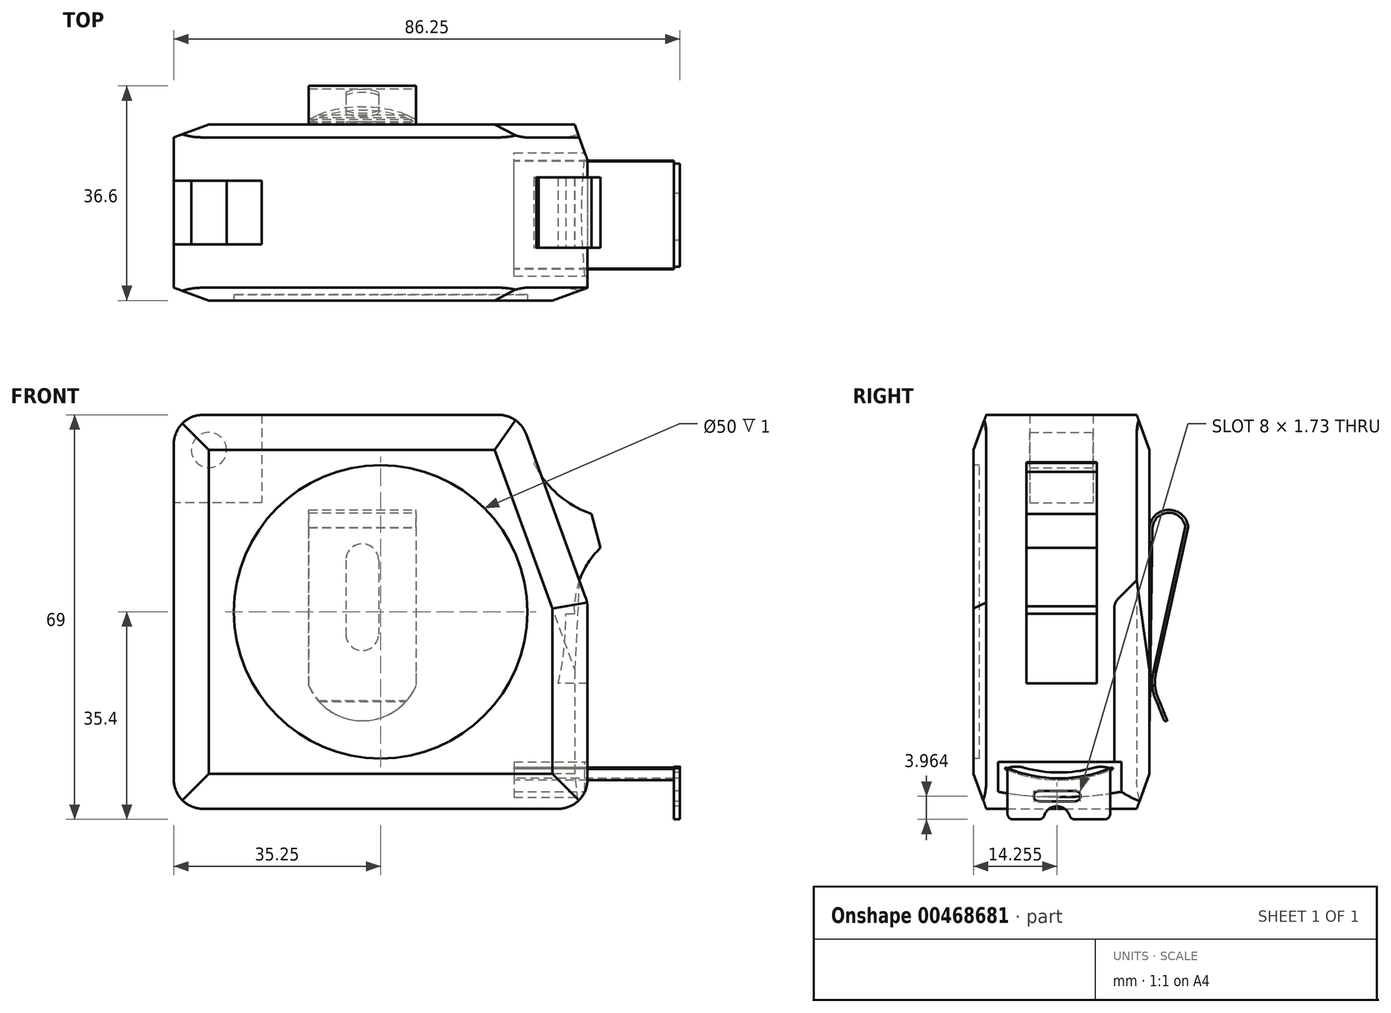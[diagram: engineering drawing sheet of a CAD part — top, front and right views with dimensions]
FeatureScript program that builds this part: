
annotation { "Feature Type Name" : "Feature", "Feature Type Description" : "" }
export const myFeature = defineFeature(function(context is Context, id is Id, definition is map)
    precondition{}
    {
        {
            var Q0;
            Q0=qCreatedBy(makeId("Front.planeOp"),FACE);
            var sketch = newSketch(context, id + "F0", { "sketchPlane" : qUnion([Q0])});
            skLineSegment(sketch, "E0.bottom", {"start": v(35.25, -33.6) * mm, "end": v(-35.25, -33.6) * mm});
            skLineSegment(sketch, "E0.top", {"start": v(35.25, 33.6) * mm, "end": v(-35.25, 33.6) * mm});
            skLineSegment(sketch, "E0.left", {"start": v(35.25, -33.6) * mm, "end": v(35.25, 33.6) * mm});
            skLineSegment(sketch, "E0.right", {"start": v(-35.25, -33.6) * mm, "end": v(-35.25, 33.6) * mm});
            skPoint(sketch, "E0.middle", {"position": v(0, 0) * mm});
            skSolve(sketch);
        }
        {
            var Q0;
            Q0 = qSketchRegion(id + "F0", true);
            extrude(context, id + "F1", {"entities" : qUnion([Q0]), "endBound" : BoundingType.SYMMETRIC, "depth" : 30 * mm});
        }
        {
            var Q0;
            Q0=makeQuery(id+"F1.opExtrude","SWEPT_EDGE",EDGE,{"disambiguationData":[OSD([sQuery(id+"F0.wireOp",EDGE,"E0.top"),sQuery(id+"F0.wireOp",EDGE,"E0.left")])]});
            chamfer(context, id + "F2", {"entities" : qUnion([Q0]), "chamferType" : ChamferType.OFFSET_ANGLE, "width" : 32 * mm, "oppositeDirection" : true, "angle" : 20 * degree, "tangentPropagation" : true});
        }
        {
            var Q0;
            Q0=makeQuery(id+"F1.opExtrude","CAP_FACE",FACE,{"disambiguationData":[OSD([sQuery(id+"F0.wireOp",EDGE,"E0.bottom"),sQuery(id+"F0.wireOp",EDGE,"E0.top"),sQuery(id+"F0.wireOp",EDGE,"E0.left"),sQuery(id+"F0.wireOp",EDGE,"E0.right")])],"isStart":false});
            var sketch = newSketch(context, id + "F3", { "sketchPlane" : qUnion([Q0])});
            skCircle(sketch, "E1", {"center": v(0, 0) * mm, "radius": 25 * mm});
            skSolve(sketch);
        }
        {
            var Q0;
            Q0 = qSketchRegion(id + "F3", true);
            extrude(context, id + "F4", {"entities" : qUnion([Q0]), "operationType" : NewBodyOperationType.REMOVE, "oppositeDirection" : true, "depth" : 1 * mm});
        }
        {
            var Q0;
            Q0=makeQuery(id+"F1.opExtrude","CAP_FACE",FACE,{"disambiguationData":[OSD([sQuery(id+"F0.wireOp",EDGE,"E0.bottom"),sQuery(id+"F0.wireOp",EDGE,"E0.top"),sQuery(id+"F0.wireOp",EDGE,"E0.left"),sQuery(id+"F0.wireOp",EDGE,"E0.right")])],"isStart":true});
            var sketch = newSketch(context, id + "F5", { "sketchPlane" : qUnion([Q0])});
            skLineSegment(sketch, "E2.bottom", {"start": v(-6.05, 17.4) * mm, "end": v(12.25, 17.4) * mm});
            skLineSegment(sketch, "E2.left", {"start": v(-6.05, 17.4) * mm, "end": v(-6.05, -12.6) * mm});
            skLineSegment(sketch, "E2.right", {"start": v(12.25, 17.4) * mm, "end": v(12.25, -12.6) * mm});
            skArc(sketch, "E3", {"start": v(-6.05, -12.6) * mm, "mid": v(3.1, -18.6) * mm, "end": v(12.25, -12.6) * mm});
            skLineSegment(sketch, "E4.left", {"start": v(5.93, -3.8) * mm, "end": v(5.93, 8.8) * mm});
            skLineSegment(sketch, "E4.right", {"start": v(0.35, -3.8) * mm, "end": v(0.35, 8.8) * mm});
            skPoint(sketch, "E4.middle", {"position": v(3.14, 2.5) * mm});
            skArc(sketch, "E5", {"start": v(0.35, -3.8) * mm, "mid": v(3.14, -6.6) * mm, "end": v(5.93, -3.8) * mm});
            skArc(sketch, "E6", {"start": v(0.35, 8.8) * mm, "mid": v(3.14, 11.6) * mm, "end": v(5.93, 8.8) * mm});
            skSolve(sketch);
        }
        {
            var Q0;
            Q0 = qSketchRegion(id + "F5", true);
            extrude(context, id + "F6", {"entities" : qUnion([Q0]), "operationType" : NewBodyOperationType.ADD, "depth" : 6.6 * mm});
        }
        {
            var Q0;
            Q0=makeQuery(id+"F6.opExtrude","SWEPT_FACE",FACE,{"disambiguationData":[OSD([sQuery(id+"F5.wireOp",EDGE,"E2.left")])]});
            var sketch = newSketch(context, id + "F7", { "sketchPlane" : qUnion([Q0])});
            skSolve(sketch);
        }
        {
            var Q0;
            {var subQ0=sQuery(id+"F5.wireOp",EDGE,"E2.left");Q0=makeQuery(id+"F7.imprint","IMPRINT",FACE,{"disambiguationData":[TD([[makeQuery(id+"F7.imprint","IMPRINT",EDGE,{"derivedFrom":makeQuery(id+"F6.opExtrude","CAP_EDGE",EDGE,{"disambiguationData":[OSD([subQ0])],"isStart":false})}),-1.0]])]});}
            var sketch = newSketch(context, id + "F8", { "sketchPlane" : qUnion([Q0])});
            skLineSegment(sketch, "E7.bottom", {"start": v(21.6, 17.4) * mm, "end": v(15, 17.4) * mm});
            skLineSegment(sketch, "E7.left", {"start": v(21.6, 17.4) * mm, "end": v(21.6, 14.4) * mm});
            skLineSegment(sketch, "E7.right", {"start": v(15, 17.4) * mm, "end": v(15, 14.4) * mm});
            skArc(sketch, "E8", {"start": v(21.6, 14.4) * mm, "mid": v(18.3, 17.4) * mm, "end": v(15, 14.4) * mm});
            skLineSegment(sketch, "E9", {"start": v(21.6, 14.4) * mm, "end": v(16.08, -10.55) * mm});
            skArc(sketch, "E10", {"start": v(16.08, -10.55) * mm, "mid": v(15.98, -12.89) * mm, "end": v(16.66, -15.12) * mm});
            skLineSegment(sketch, "E11", {"start": v(16.66, -15.12) * mm, "end": v(18.33, -19.28) * mm});
            skArc(sketch, "E12.0", {"start": v(21.1, 14.43) * mm, "mid": v(18.26, 16.9) * mm, "end": v(15.5, 14.35) * mm});
            skLineSegment(sketch, "E12.1", {"start": v(21.1, 14.43) * mm, "end": v(15.6, -10.44) * mm});
            skArc(sketch, "E12.2", {"start": v(15.6, -10.44) * mm, "mid": v(15.48, -12.94) * mm, "end": v(16.2, -15.33) * mm});
            skLineSegment(sketch, "E12.3", {"start": v(16.2, -15.33) * mm, "end": v(17.86, -19.47) * mm});
            skLineSegment(sketch, "E13", {"start": v(18.33, -19.28) * mm, "end": v(22.1, -19.28) * mm});
            skLineSegment(sketch, "E14", {"start": v(22.1, -19.28) * mm, "end": v(21.6, 14.4) * mm});
            skLineSegment(sketch, "E15", {"start": v(15.5, 14.35) * mm, "end": v(15, -19.72) * mm});
            skLineSegment(sketch, "E16", {"start": v(15, -19.72) * mm, "end": v(17.86, -19.47) * mm});
            skSolve(sketch);
        }
        {
            var Q0;
            Q0 = qSketchRegion(id + "F8", true);
            extrude(context, id + "F9", {"entities" : qUnion([Q0]), "operationType" : NewBodyOperationType.REMOVE, "oppositeDirection" : true, "depth" : 25 * mm});
        }
        {
            var Q0;
            Q0=makeQuery(id+"F1.opExtrude","CAP_EDGE",EDGE,{"disambiguationData":[OSD([sQuery(id+"F0.wireOp",EDGE,"E0.top")])],"isStart":false});
            var Q1;
            Q1=makeQuery(id+"F1.opExtrude","CAP_EDGE",EDGE,{"disambiguationData":[OSD([sQuery(id+"F0.wireOp",EDGE,"E0.top")])],"isStart":true});
            var Q2;
            {var subQ0=sQuery(id+"F0.wireOp",EDGE,"E0.left");var subQ1=sQuery(id+"F0.wireOp",EDGE,"E0.top");Q2=makeQuery(id+"F2.opChamfer","BLEND_EDGE",EDGE,{"blendedFrom":[makeQuery(id+"F1.opExtrude","SWEPT_EDGE",EDGE,{"disambiguationData":[OSD([subQ1,subQ0])]}),makeQuery(id+"F1.opExtrude","CAP_FACE",FACE,{"disambiguationData":[OSD([sQuery(id+"F0.wireOp",EDGE,"E0.bottom"),subQ1,subQ0,sQuery(id+"F0.wireOp",EDGE,"E0.right")])],"isStart":false})],"blendedInto":[makeQuery(id+"F1.opExtrude","CAP_FACE",FACE,{"disambiguationData":[OSD([sQuery(id+"F0.wireOp",EDGE,"E0.bottom"),subQ1,subQ0,sQuery(id+"F0.wireOp",EDGE,"E0.right")])],"isStart":false})]});}
            var Q3;
            Q3=makeQuery(id+"F1.opExtrude","CAP_EDGE",EDGE,{"disambiguationData":[OSD([sQuery(id+"F0.wireOp",EDGE,"E0.left")])],"isStart":false});
            var Q4;
            Q4=makeQuery(id+"F1.opExtrude","CAP_EDGE",EDGE,{"disambiguationData":[OSD([sQuery(id+"F0.wireOp",EDGE,"E0.bottom")])],"isStart":true});
            var Q5;
            Q5=makeQuery(id+"F1.opExtrude","CAP_EDGE",EDGE,{"disambiguationData":[OSD([sQuery(id+"F0.wireOp",EDGE,"E0.bottom")])],"isStart":false});
            var Q6;
            Q6=makeQuery(id+"F1.opExtrude","CAP_EDGE",EDGE,{"disambiguationData":[OSD([sQuery(id+"F0.wireOp",EDGE,"E0.right")])],"isStart":false});
            var Q7;
            Q7=makeQuery(id+"F1.opExtrude","CAP_EDGE",EDGE,{"disambiguationData":[OSD([sQuery(id+"F0.wireOp",EDGE,"E0.right")])],"isStart":true});
            var Q8;
            {var subQ0=sQuery(id+"F0.wireOp",EDGE,"E0.left");var subQ1=sQuery(id+"F0.wireOp",EDGE,"E0.top");Q8=makeQuery(id+"F2.opChamfer","BLEND_EDGE",EDGE,{"blendedFrom":[makeQuery(id+"F1.opExtrude","SWEPT_EDGE",EDGE,{"disambiguationData":[OSD([subQ1,subQ0])]}),makeQuery(id+"F1.opExtrude","CAP_FACE",FACE,{"disambiguationData":[OSD([sQuery(id+"F0.wireOp",EDGE,"E0.bottom"),subQ1,subQ0,sQuery(id+"F0.wireOp",EDGE,"E0.right")])],"isStart":true})],"blendedInto":[makeQuery(id+"F1.opExtrude","CAP_FACE",FACE,{"disambiguationData":[OSD([sQuery(id+"F0.wireOp",EDGE,"E0.bottom"),subQ1,subQ0,sQuery(id+"F0.wireOp",EDGE,"E0.right")])],"isStart":true})]});}
            var Q9;
            Q9=makeQuery(id+"F1.opExtrude","CAP_EDGE",EDGE,{"disambiguationData":[OSD([sQuery(id+"F0.wireOp",EDGE,"E0.left")])],"isStart":true});
            chamfer(context, id + "F10", {"entities" : qUnion([Q0, Q1, Q2, Q3, Q4, Q5, Q6, Q7, Q8, Q9]), "chamferType" : ChamferType.OFFSET_ANGLE, "width" : 6 * mm, "oppositeDirection" : false, "angle" : 20 * degree, "tangentPropagation" : true});
        }
        {
            var Q0;
            Q0=makeQuery(id+"F1.opExtrude","SWEPT_EDGE",EDGE,{"disambiguationData":[OSD([sQuery(id+"F0.wireOp",EDGE,"E0.top"),sQuery(id+"F0.wireOp",EDGE,"E0.right")])]});
            var Q1;
            {var subQ0=sQuery(id+"F0.wireOp",EDGE,"E0.top");Q1=makeQuery(id+"F2.opChamfer","BLEND_EDGE",EDGE,{"blendedFrom":[makeQuery(id+"F1.opExtrude","SWEPT_EDGE",EDGE,{"disambiguationData":[OSD([subQ0,sQuery(id+"F0.wireOp",EDGE,"E0.left")])]}),makeQuery(id+"F1.opExtrude","SWEPT_FACE",FACE,{"disambiguationData":[OSD([subQ0])]})],"blendedInto":[makeQuery(id+"F1.opExtrude","SWEPT_FACE",FACE,{"disambiguationData":[OSD([subQ0])]})]});}
            var Q2;
            {var subQ0=sQuery(id+"F0.wireOp",EDGE,"E0.left");Q2=makeQuery(id+"F2.opChamfer","BLEND_EDGE",EDGE,{"blendedFrom":[makeQuery(id+"F1.opExtrude","SWEPT_EDGE",EDGE,{"disambiguationData":[OSD([sQuery(id+"F0.wireOp",EDGE,"E0.top"),subQ0])]}),makeQuery(id+"F1.opExtrude","SWEPT_FACE",FACE,{"disambiguationData":[OSD([subQ0])]})],"blendedInto":[makeQuery(id+"F1.opExtrude","SWEPT_FACE",FACE,{"disambiguationData":[OSD([subQ0])]})]});}
            var Q3;
            Q3=makeQuery(id+"F1.opExtrude","SWEPT_EDGE",EDGE,{"disambiguationData":[OSD([sQuery(id+"F0.wireOp",EDGE,"E0.bottom"),sQuery(id+"F0.wireOp",EDGE,"E0.left")])]});
            var Q4;
            Q4=makeQuery(id+"F1.opExtrude","SWEPT_EDGE",EDGE,{"disambiguationData":[OSD([sQuery(id+"F0.wireOp",EDGE,"E0.bottom"),sQuery(id+"F0.wireOp",EDGE,"E0.right")])]});
            fillet(context, id + "F11", {"entities" : qUnion([Q0, Q1, Q2, Q3, Q4]), "radius" : 5 * mm, "tangentPropagation" : true, "allowEdgeOverflow" : false});
        }
        {
            var Q0;
            Q0=qCreatedBy(makeId("Front.planeOp"),FACE);
            var sketch = newSketch(context, id + "F12", { "sketchPlane" : qUnion([Q0])});
            skLineSegment(sketch, "E17.bottom", {"start": v(-20.25, 33.6) * mm, "end": v(-35.25, 33.6) * mm});
            skLineSegment(sketch, "E17.top", {"start": v(-20.25, 18.6) * mm, "end": v(-35.25, 18.6) * mm});
            skLineSegment(sketch, "E17.left", {"start": v(-20.25, 33.6) * mm, "end": v(-20.25, 18.6) * mm});
            skLineSegment(sketch, "E17.right", {"start": v(-35.25, 33.6) * mm, "end": v(-35.25, 18.6) * mm});
            skCircle(sketch, "E18", {"center": v(-29.25, 27.6) * mm, "radius": 3 * mm});
            skSolve(sketch);
        }
        {
            var Q0;
            Q0 = qSketchRegion(id + "F12", true);
            extrude(context, id + "F13", {"entities" : qUnion([Q0]), "operationType" : NewBodyOperationType.REMOVE, "endBound" : BoundingType.SYMMETRIC, "depth" : 10.8 * mm});
        }
        {
            var Q0;
            Q0=qCreatedBy(makeId("Front.planeOp"),FACE);
            var sketch = newSketch(context, id + "F14", { "sketchPlane" : qUnion([Q0])});
            skLineSegment(sketch, "E19", {"start": v(26.54, 25.54) * mm, "end": v(35.25, 1.6) * mm});
            skLineSegment(sketch, "E20", {"start": v(35.25, 1.6) * mm, "end": v(35.25, -12.2) * mm});
            skLineSegment(sketch, "E21", {"start": v(35.25, -12.2) * mm, "end": v(30.25, -12.2) * mm});
            skLineSegment(sketch, "E22", {"start": v(26.09, 25.38) * mm, "end": v(24.66, 24.86) * mm});
            skArc(sketch, "E23", {"start": v(30.25, -12.2) * mm, "mid": v(30.99, 6.86) * mm, "end": v(24.66, 24.86) * mm});
            skArc(sketch, "E24", {"start": v(31.56, -0.35) * mm, "mid": v(29.75, 12.7) * mm, "end": v(24.66, 24.86) * mm});
            skArc(sketch, "E25.0", {"start": v(33.06, -0.34) * mm, "mid": v(33.05, 0.3) * mm, "end": v(33.03, 0.94) * mm});
            skLineSegment(sketch, "E26", {"start": v(24.66, 24.86) * mm, "end": v(26.09, 25.38) * mm});
            skLineSegment(sketch, "E27", {"start": v(31.56, -0.35) * mm, "end": v(33.06, -0.34) * mm});
            skLineSegment(sketch, "E28", {"start": v(35.95, 16.7) * mm, "end": v(37.46, 10.9) * mm});
            skPoint(sketch, "E29.start.orphan", {"position": v(36.9, 13.85) * mm});
            skArc(sketch, "E30", {"start": v(37.46, 10.9) * mm, "mid": v(34, 5.77) * mm, "end": v(33.06, -0.34) * mm});
            skArc(sketch, "E31", {"start": v(26.09, 25.38) * mm, "mid": v(30.15, 20.05) * mm, "end": v(35.95, 16.7) * mm});
            skPoint(sketch, "E32.0.end.orphan", {"position": v(33.23, 27.97) * mm});
            skPoint(sketch, "E33.orphan", {"position": v(40.56, -0.28) * mm});
            skArc(sketch, "E34.trimOffspring", {"start": v(27.7, 22.36) * mm, "mid": v(26.92, 23.88) * mm, "end": v(26.09, 25.38) * mm});
            skLineSegment(sketch, "E35", {"start": v(26.09, 25.38) * mm, "end": v(26.54, 25.54) * mm});
            skSolve(sketch);
        }
        {
            var Q0;
            {var subQ0=sQuery(id+"F14.wireOp",EDGE,"E35");Q0=makeQuery(id+"F14.imprint","IMPRINT",FACE,{"disambiguationData":[TD([[makeQuery(id+"F14.imprint","IMPRINT",EDGE,{"derivedFrom":subQ0}),-1.0]])]});}
            var Q1;
            {var subQ0=sQuery(id+"F14.wireOp",EDGE,"E20");Q1=makeQuery(id+"F14.imprint","IMPRINT",FACE,{"disambiguationData":[TD([[makeQuery(id+"F14.imprint","IMPRINT",EDGE,{"derivedFrom":subQ0}),-1.0]])]});}
            extrude(context, id + "F15", {"entities" : qUnion([Q0, Q1]), "operationType" : NewBodyOperationType.REMOVE, "endBound" : BoundingType.SYMMETRIC, "oppositeDirection" : true, "depth" : 12 * mm});
        }
        {
            var Q0;
            {var subQ1=sQuery(id+"F14.wireOp",EDGE,"E28");Q0=makeQuery(id+"F14.imprint","IMPRINT",FACE,{"disambiguationData":[TD([[makeQuery(id+"F14.imprint","IMPRINT",EDGE,{"derivedFrom":subQ1}),-1.0]])]});}
            extrude(context, id + "F16", {"entities" : qUnion([Q0]), "operationType" : NewBodyOperationType.ADD, "endBound" : BoundingType.SYMMETRIC, "depth" : 12 * mm});
        }
        {
            var Q0;
            Q0=makeQuery(id+"F1.opExtrude","SWEPT_FACE",FACE,{"disambiguationData":[OSD([sQuery(id+"F0.wireOp",EDGE,"E0.left")])]});
            var sketch = newSketch(context, id + "F17", { "sketchPlane" : qUnion([Q0])});
            skPoint(sketch, "E36.start.orphan", {"position": v(4.25, -24.41) * mm});
            skPoint(sketch, "E37.start.orphan", {"position": v(-1.9, -24.5) * mm});
            skArc(sketch, "E38", {"start": v(-10.82, -30.7) * mm, "mid": v(-0.32, -31.6) * mm, "end": v(10.18, -30.7) * mm});
            skLineSegment(sketch, "E39", {"start": v(-10.82, -25.6) * mm, "end": v(10.18, -25.6) * mm});
            skLineSegment(sketch, "E40", {"start": v(10.18, -25.6) * mm, "end": v(10.18, -30.7) * mm});
            skLineSegment(sketch, "E41", {"start": v(-10.82, -25.6) * mm, "end": v(-10.82, -30.7) * mm});
            skSolve(sketch);
        }
        {
            var Q0;
            Q0 = qSketchRegion(id + "F17", true);
            extrude(context, id + "F18", {"entities" : qUnion([Q0]), "operationType" : NewBodyOperationType.REMOVE, "endBound" : BoundingType.SYMMETRIC, "oppositeDirection" : true, "depth" : 25 * mm});
        }
        {
            var Q0;
            Q0=qCreatedBy(makeId("Right.planeOp"),FACE);
            var sketch = newSketch(context, id + "F19", { "sketchPlane" : qUnion([Q0])});
            skArc(sketch, "E42", {"start": v(-9.55, -26.52) * mm, "mid": v(-0.42, -28.4) * mm, "end": v(8.71, -26.52) * mm});
            skArc(sketch, "E43.0", {"start": v(-9.66, -26.8) * mm, "mid": v(-0.42, -28.7) * mm, "end": v(8.83, -26.8) * mm});
            skLineSegment(sketch, "E44", {"start": v(-9.55, -26.52) * mm, "end": v(-9.66, -26.8) * mm});
            skLineSegment(sketch, "E45", {"start": v(8.71, -26.52) * mm, "end": v(8.83, -26.8) * mm});
            skSolve(sketch);
        }
        {
            var Q0;
            Q0 = qSketchRegion(id + "F19", true);
            extrude(context, id + "F20", {"entities" : qUnion([Q0]), "operationType" : NewBodyOperationType.ADD, "depth" : 50 * mm});
        }
        {
            var Q0;
            Q0=makeQuery(id+"F20.opExtrude","CAP_FACE",FACE,{"disambiguationData":[OSD([sQuery(id+"F19.wireOp",EDGE,"E42"),sQuery(id+"F19.wireOp",EDGE,"E43.0"),sQuery(id+"F19.wireOp",EDGE,"E44"),sQuery(id+"F19.wireOp",EDGE,"E45")])],"isStart":false});
            var sketch = newSketch(context, id + "F21", { "sketchPlane" : qUnion([Q0])});
            skArc(sketch, "E46", {"start": v(-9.55, -26.52) * mm, "mid": v(-0.42, -28.4) * mm, "end": v(8.71, -26.52) * mm});
            skArc(sketch, "E47.0", {"start": v(-9.23, -25.57) * mm, "mid": v(-0.46, -27.4) * mm, "end": v(8.32, -25.6) * mm});
            skLineSegment(sketch, "E48", {"start": v(-9.23, -35.4) * mm, "end": v(8.32, -35.4) * mm});
            skLineSegment(sketch, "E49", {"start": v(8.32, -35.4) * mm, "end": v(8.32, -25.6) * mm});
            skLineSegment(sketch, "E50", {"start": v(-9.23, -25.57) * mm, "end": v(-9.23, -35.4) * mm});
            skLineSegment(sketch, "E51.bottom", {"start": v(-3.88, -30.57) * mm, "end": v(2.4, -30.57) * mm});
            skLineSegment(sketch, "E51.top", {"start": v(-3.88, -32.3) * mm, "end": v(2.4, -32.3) * mm});
            skArc(sketch, "E52", {"start": v(2.4, -32.3) * mm, "mid": v(3.25, -31.44) * mm, "end": v(2.4, -30.57) * mm});
            skArc(sketch, "E53", {"start": v(-3.88, -30.57) * mm, "mid": v(-4.75, -31.44) * mm, "end": v(-3.88, -32.3) * mm});
            skArc(sketch, "E54", {"start": v(1.47, -35.4) * mm, "mid": v(-0.78, -33.17) * mm, "end": v(-3.02, -35.4) * mm});
            skSolve(sketch);
        }
        {
            var Q0;
            Q0=makeQuery(id+"F21.imprint","IMPRINT",FACE,{"disambiguationData":[TD([[makeQuery(id+"F21.imprint","IMPRINT",EDGE,{"derivedFrom":sQuery(id+"F21.wireOp",EDGE,"E51.bottom")}),1.0]])]});
            var Q1;
            {var subQ0=sQuery(id+"F21.wireOp",EDGE,"E47.0");Q1=makeQuery(id+"F21.imprint","IMPRINT",FACE,{"disambiguationData":[TD([[makeQuery(id+"F21.imprint","IMPRINT",EDGE,{"derivedFrom":subQ0}),-1.0]])]});}
            var Q2;
            {var subQ0=sQuery(id+"F21.wireOp",EDGE,"E50");var subQ1=sQuery(id+"F21.wireOp",EDGE,"E46");var subQ2=makeQuery(id+"F21.imprint","INTERSECT",VERTEX,{"derivedFrom":[subQ1,subQ0]});Q2=makeQuery(id+"F21.imprint","IMPRINT",FACE,{"disambiguationData":[TD([[makeQuery(id+"F21.imprint","IMPRINT",EDGE,{"disambiguationData":[TD([[subQ2,-1.0]])],"derivedFrom":subQ1}),-1.0]])]});}
            extrude(context, id + "F22", {"entities" : qUnion([Q0, Q1, Q2]), "operationType" : NewBodyOperationType.ADD, "depth" : 1 * mm});
        }
        {
            var Q0;
            Q0=makeQuery(id+"F22.opExtrude","SWEPT_EDGE",EDGE,{"disambiguationData":[OSD([sQuery(id+"F21.wireOp",EDGE,"E47.0"),sQuery(id+"F21.wireOp",EDGE,"E50")])]});
            var Q1;
            Q1=makeQuery(id+"F22.opExtrude","SWEPT_EDGE",EDGE,{"disambiguationData":[OSD([sQuery(id+"F21.wireOp",EDGE,"E47.0"),sQuery(id+"F21.wireOp",EDGE,"E49")])]});
            fillet(context, id + "F23", {"entities" : qUnion([Q0, Q1]), "radius" : 5 * mm, "tangentPropagation" : true, "allowEdgeOverflow" : false});
        }
        {
            var Q0;
            Q0=makeQuery(id+"F22.opExtrude","SWEPT_EDGE",EDGE,{"disambiguationData":[OSD([sQuery(id+"F21.wireOp",EDGE,"E48"),sQuery(id+"F21.wireOp",EDGE,"E50")])]});
            var Q1;
            Q1=makeQuery(id+"F22.opExtrude","SWEPT_EDGE",EDGE,{"disambiguationData":[OSD([sQuery(id+"F21.wireOp",EDGE,"E48"),sQuery(id+"F21.wireOp",EDGE,"E49")])]});
            var Q2;
            {var subQ0=sQuery(id+"F21.wireOp",EDGE,"E54");var subQ1=sQuery(id+"F21.wireOp",EDGE,"E48");Q2=makeQuery(id+"F22.opExtrude","SWEPT_EDGE",EDGE,{"disambiguationData":[OSD([subQ1,subQ0]),TDD([makeQuery(id+"F21.imprint","INTERSECT",VERTEX,{"disambiguationData":[OD(0.0)],"derivedFrom":[subQ1,subQ0]})])]});}
            var Q3;
            {var subQ0=sQuery(id+"F21.wireOp",EDGE,"E54");var subQ1=sQuery(id+"F21.wireOp",EDGE,"E48");Q3=makeQuery(id+"F22.opExtrude","SWEPT_EDGE",EDGE,{"disambiguationData":[OSD([subQ1,subQ0]),TDD([makeQuery(id+"F21.imprint","INTERSECT",VERTEX,{"disambiguationData":[OD(1.0)],"derivedFrom":[subQ1,subQ0]})])]});}
            fillet(context, id + "F24", {"entities" : qUnion([Q0, Q1, Q2, Q3]), "radius" : 1 * mm, "tangentPropagation" : true, "allowEdgeOverflow" : false});
        }
    });
